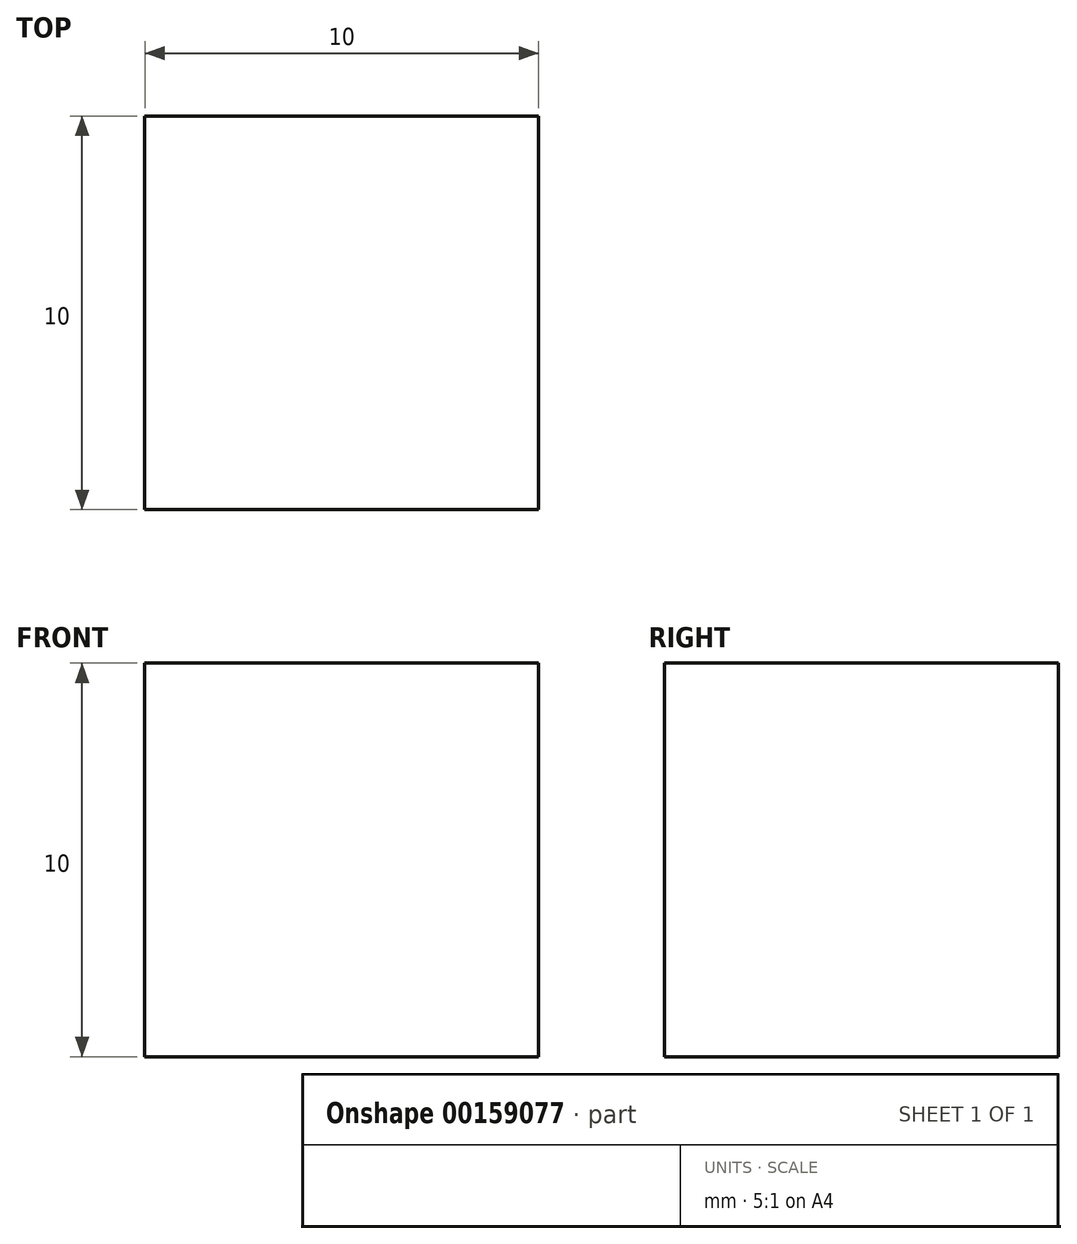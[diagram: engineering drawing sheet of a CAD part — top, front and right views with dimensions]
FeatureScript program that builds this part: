
annotation { "Feature Type Name" : "Feature", "Feature Type Description" : "" }
export const myFeature = defineFeature(function(context is Context, id is Id, definition is map)
    precondition{}
    {
        {
            var Q0;
            Q0=qCreatedBy(makeId("Top.planeOp"),FACE);
            var sketch = newSketch(context, id + "F0", { "sketchPlane" : qUnion([Q0])});
            skLineSegment(sketch, "E0.bottom", {"start": v(-18.7, 0) * mm, "end": v(-8.7, 0) * mm});
            skLineSegment(sketch, "E0.top", {"start": v(-18.7, -10) * mm, "end": v(-8.7, -10) * mm});
            skLineSegment(sketch, "E0.left", {"start": v(-18.7, 0) * mm, "end": v(-18.7, -10) * mm});
            skLineSegment(sketch, "E0.right", {"start": v(-8.7, 0) * mm, "end": v(-8.7, -10) * mm});
            skSolve(sketch);
        }
        {
            var Q0;
            Q0 = qSketchRegion(id + "F0", true);
            extrude(context, id + "F1", {"entities" : qUnion([Q0]), "depth" : 10 * mm});
        }
    });
